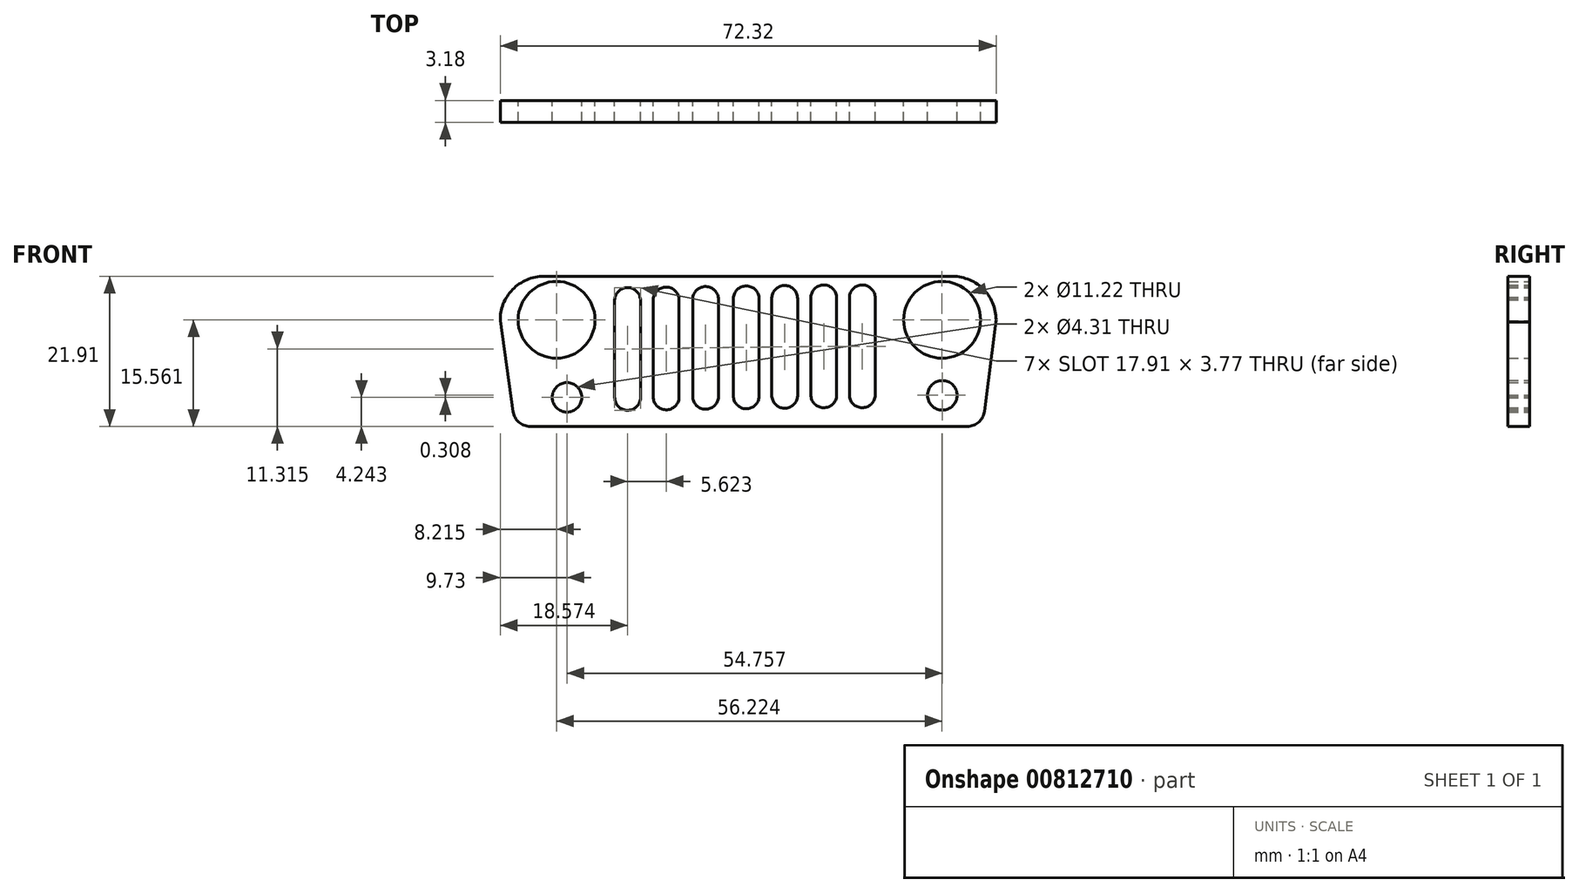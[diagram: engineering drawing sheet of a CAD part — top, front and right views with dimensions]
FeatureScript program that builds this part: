
annotation { "Feature Type Name" : "Feature", "Feature Type Description" : "" }
export const myFeature = defineFeature(function(context is Context, id is Id, definition is map)
    precondition{}
    {
        {
            var Q0;
            Q0=qCreatedBy(makeId("Front.planeOp"),FACE);
            var sketch = newSketch(context, id + "F0", { "sketchPlane" : qUnion([Q0])});
            skLineSegment(sketch, "E0.bottom", {"start": v(-40.14, 38.3) * mm, "end": v(19.48, 38.3) * mm});
            skLineSegment(sketch, "E0.top", {"start": v(-42.11, 16.4) * mm, "end": v(21.62, 16.4) * mm});
            skArc(sketch, "E1.filletArc", {"start": v(-40.14, 38.3) * mm, "mid": v(-44.69, 36.39) * mm, "end": v(-46.5, 31.8) * mm});
            skPoint(sketch, "E2.visualSharp", {"position": v(30.06, 38.3) * mm});
            skArc(sketch, "E2.filletArc", {"start": v(25.82, 31.64) * mm, "mid": v(24.08, 36.33) * mm, "end": v(19.48, 38.3) * mm});
            skLineSegment(sketch, "E3", {"start": v(-46.5, 31.8) * mm, "end": v(-44.63, 18.58) * mm});
            skLineSegment(sketch, "E4", {"start": v(25.82, 31.64) * mm, "end": v(24.14, 18.6) * mm});
            skArc(sketch, "E5.filletArc", {"start": v(-44.63, 18.58) * mm, "mid": v(-43.78, 17.02) * mm, "end": v(-42.11, 16.4) * mm});
            skArc(sketch, "E6.filletArc", {"start": v(21.62, 16.4) * mm, "mid": v(23.3, 17.03) * mm, "end": v(24.14, 18.6) * mm});
            skCircle(sketch, "E7", {"center": v(-38.27, 31.95) * mm, "radius": 5.6 * mm});
            skArc(sketch, "E8", {"start": v(-25.78, 20.56) * mm, "mid": v(-25.77, 20.5) * mm, "end": v(-25.75, 20.45) * mm});
            skLineSegment(sketch, "E9", {"start": v(-29.8, 34.85) * mm, "end": v(-29.8, 20.56) * mm});
            skLineSegment(sketch, "E10", {"start": v(-26.03, 20.56) * mm, "end": v(-26.03, 34.78) * mm});
            skArc(sketch, "E11", {"start": v(-26.03, 34.78) * mm, "mid": v(-27.88, 36.66) * mm, "end": v(-29.8, 34.85) * mm});
            skArc(sketch, "E12", {"start": v(-29.8, 20.63) * mm, "mid": v(-27.95, 18.75) * mm, "end": v(-26.03, 20.56) * mm});
            skLineSegment(sketch, "E13", {"start": v(-24.18, 34.93) * mm, "end": v(-24.18, 20.63) * mm});
            skLineSegment(sketch, "E14", {"start": v(-20.4, 20.63) * mm, "end": v(-20.4, 34.85) * mm});
            skArc(sketch, "E15", {"start": v(-20.4, 34.85) * mm, "mid": v(-22.26, 36.74) * mm, "end": v(-24.18, 34.93) * mm});
            skArc(sketch, "E16", {"start": v(-24.18, 20.7) * mm, "mid": v(-22.33, 18.83) * mm, "end": v(-20.4, 20.63) * mm});
            skLineSegment(sketch, "E17", {"start": v(-18.42, 35) * mm, "end": v(-18.42, 20.7) * mm});
            skLineSegment(sketch, "E18", {"start": v(-14.65, 20.7) * mm, "end": v(-14.65, 34.93) * mm});
            skArc(sketch, "E19", {"start": v(-14.65, 34.93) * mm, "mid": v(-16.5, 36.81) * mm, "end": v(-18.42, 35) * mm});
            skArc(sketch, "E20", {"start": v(-18.42, 20.79) * mm, "mid": v(-16.57, 18.9) * mm, "end": v(-14.65, 20.7) * mm});
            skLineSegment(sketch, "E21", {"start": v(-12.5, 35.08) * mm, "end": v(-12.5, 20.79) * mm});
            skLineSegment(sketch, "E22", {"start": v(-8.73, 20.79) * mm, "end": v(-8.73, 35) * mm});
            skArc(sketch, "E23", {"start": v(-8.73, 35) * mm, "mid": v(-10.57, 36.9) * mm, "end": v(-12.5, 35.08) * mm});
            skArc(sketch, "E24", {"start": v(-12.5, 20.86) * mm, "mid": v(-10.65, 18.98) * mm, "end": v(-8.73, 20.79) * mm});
            skLineSegment(sketch, "E25", {"start": v(-6.89, 35.16) * mm, "end": v(-6.89, 20.86) * mm});
            skLineSegment(sketch, "E26", {"start": v(-3.12, 20.86) * mm, "end": v(-3.12, 35.08) * mm});
            skArc(sketch, "E27", {"start": v(-3.12, 35.08) * mm, "mid": v(-4.97, 36.97) * mm, "end": v(-6.89, 35.16) * mm});
            skArc(sketch, "E28", {"start": v(-6.89, 20.94) * mm, "mid": v(-5.04, 19.06) * mm, "end": v(-3.12, 20.86) * mm});
            skLineSegment(sketch, "E29", {"start": v(-1.19, 35.24) * mm, "end": v(-1.19, 20.94) * mm});
            skLineSegment(sketch, "E30", {"start": v(2.58, 20.94) * mm, "end": v(2.58, 35.16) * mm});
            skArc(sketch, "E31", {"start": v(2.58, 35.16) * mm, "mid": v(0.73, 37.05) * mm, "end": v(-1.19, 35.24) * mm});
            skArc(sketch, "E32", {"start": v(-1.19, 21.02) * mm, "mid": v(0.66, 19.13) * mm, "end": v(2.58, 20.94) * mm});
            skLineSegment(sketch, "E33", {"start": v(4.43, 35.24) * mm, "end": v(4.43, 20.94) * mm});
            skLineSegment(sketch, "E34", {"start": v(8.2, 20.94) * mm, "end": v(8.2, 35.16) * mm});
            skArc(sketch, "E35", {"start": v(8.2, 35.16) * mm, "mid": v(6.35, 37.05) * mm, "end": v(4.43, 35.24) * mm});
            skArc(sketch, "E36", {"start": v(4.43, 21.02) * mm, "mid": v(6.28, 19.13) * mm, "end": v(8.2, 20.94) * mm});
            skCircle(sketch, "E37", {"center": v(17.95, 31.95) * mm, "radius": 5.6 * mm});
            skCircle(sketch, "E38", {"center": v(18, 20.94) * mm, "radius": 2.16 * mm});
            skCircle(sketch, "E39", {"center": v(-36.76, 20.63) * mm, "radius": 2.16 * mm});
            skSolve(sketch);
        }
        {
            var Q0;
            Q0=makeQuery(id+"F0.imprint","IMPRINT",FACE,{"disambiguationData":[TD([[makeQuery(id+"F0.imprint","IMPRINT",EDGE,{"derivedFrom":sQuery(id+"F0.wireOp",EDGE,"E0.bottom")}),-1.0]])]});
            extrude(context, id + "F1", {"entities" : qUnion([Q0]), "depth" : 3.17 * mm, "offsetDistance" : 25.4 * mm});
        }
        {
            var Q0;
            Q0=qSketchRegion(id+"F0",true);
            extrude(context, id + "F2", {"entities" : qUnion([Q0]), "operationType" : NewBodyOperationType.ADD, "depth" : 1 / 203.2 * mm, "offsetDistance" : 25.4 * mm});
        }
        {
            var Q0;
            Q0=qSketchRegion(id+"F0",true);
            extrude(context, id + "F3", {"entities" : qUnion([Q0]), "operationType" : NewBodyOperationType.ADD, "depth" : 3.17 * mm, "offsetDistance" : 25.4 * mm});
        }
    });
